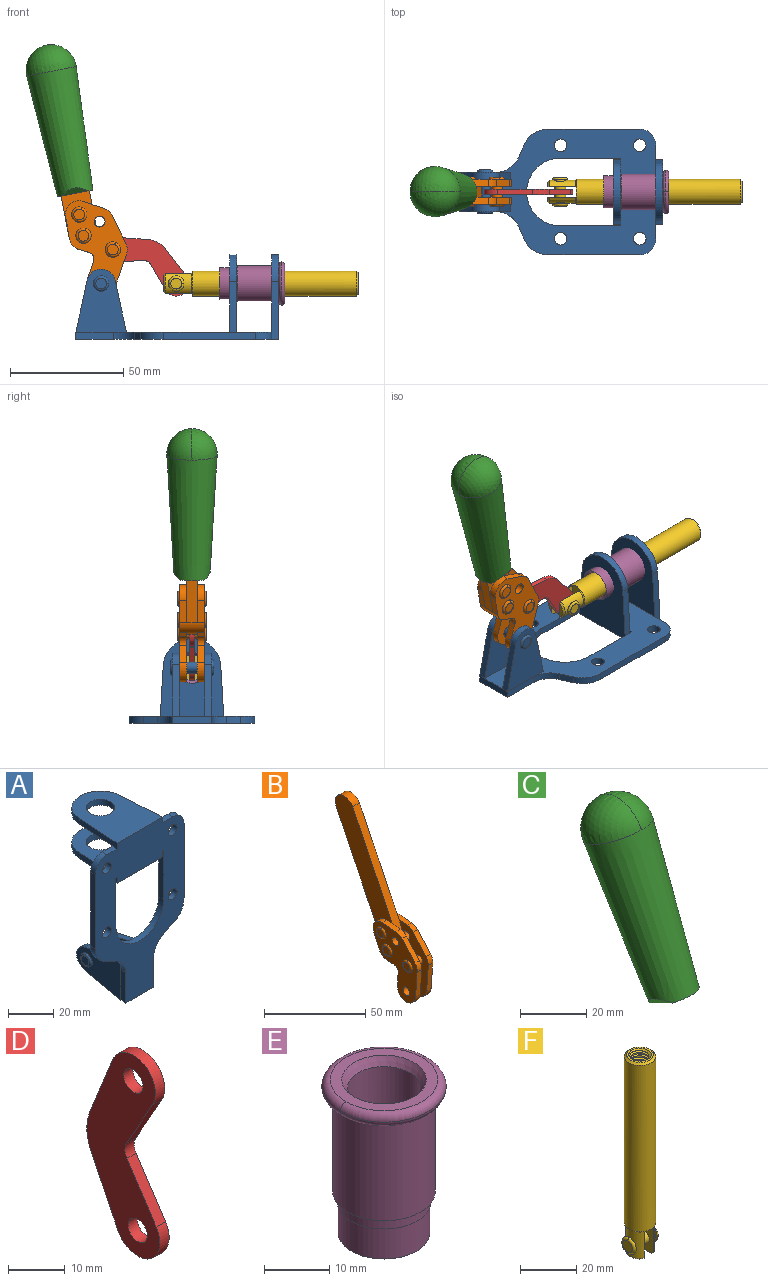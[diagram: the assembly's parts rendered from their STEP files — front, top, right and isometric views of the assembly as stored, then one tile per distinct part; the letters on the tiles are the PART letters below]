
ASSEMBLY  parts=6 mates=6
PART A: 55 faces, bbox 55.7x37.4x89.8 mm
  f0: torus R=2.41mm, axis (-1,0,0), area 15mm2, adj f11,f15,f25
  f1: torus R=2.41mm, axis (-1,0,0), area 15mm2, adj f10,f12,f22
  f2: cylinder r=2.78mm len=5.56mm, axis (0,-1,0), area 54.2mm2, adj f30,f54
  f3: cylinder r=14.99mm len=29.97mm, axis (0,-1,0), area 145.9mm2, adj f30,f49,f53,f54
  f4: cylinder r=2.78mm len=5.56mm, axis (0,-1,0), area 54.2mm2, adj f30,f54
  f5: cylinder r=2.78mm len=5.56mm, axis (0,-1,0), area 54.2mm2, adj f30,f54
  f6: cylinder r=2.78mm len=5.56mm, axis (0,-1,0), area 54.2mm2, adj f30,f54
  f7: cylinder r=6.35mm len=12.7mm, axis (0,0,1), area 123.6mm2, adj f27,f51
  f8: cylinder r=6.35mm len=12.7mm, axis (0,0,-1), area 124.7mm2, adj f21,f35
  f9: cylinder r=2.41mm len=11.18mm, axis (-1,0,0), area 169.4mm2, adj f16,f19
  f10: plane 4.83x4.83mm, normal (1,0,0), area 18.3mm2, adj f1,f12
  f11: plane 4.83x4.83mm, normal (-1,0,0), area 18.3mm2, adj f0,f15
  f12: torus R=2.41mm, axis (-1,0,0), area 15mm2, adj f1,f10,f22
  f13: cylinder r=6.35mm len=12.41mm, axis (1,0,0), area 53.4mm2, adj f18,f19,f22,f23
  f14: cylinder r=6.35mm len=12.41mm, axis (-1,0,0), area 53.4mm2, adj f16,f17,f24,f25
  f15: torus R=2.41mm, axis (-1,0,0), area 15mm2, adj f0,f11,f25
  f16: plane 27.86x22.35mm, normal (1,0,0), area 425.4mm2, adj f9,f14,f17,f24,f30
  f17: plane 22.86x4.97mm, normal (0,0.21,0.98), area 72.5mm2, adj f14,f16,f25,f30
  f18: plane 22.86x4.97mm, normal (0,0.21,0.98), area 72.5mm2, adj f13,f19,f22,f30
  f19: plane 27.86x22.35mm, normal (-1,0,0), area 425.4mm2, adj f9,f13,f18,f23,f30
  f20: cylinder r=12.7mm len=25.35mm, axis (0,0,-1), area 119.8mm2, adj f21,f34,f35,f36
  f21: plane 34.21x28.07mm, normal (0,0,-1), area 702.4mm2, adj f8,f20,f30,f34,f36
  f22: plane 27.96x22.45mm, normal (1,0,0), area 407.2mm2, adj f1,f12,f13,f18,f23,f30,f42,f43
  f23: plane 22.86x4.97mm, normal (0,0.21,-0.98), area 72.5mm2, adj f13,f19,f22,f44
  f24: plane 22.86x4.97mm, normal (0,0.21,-0.98), area 72.5mm2, adj f14,f16,f25,f44
  f25: plane 27.86x22.35mm, normal (-1,0,0), area 407.1mm2, adj f0,f14,f15,f17,f24,f30,f45,f46
  f26: plane 3.1x0.95mm, normal (0,0,-1), area 2.7mm2, adj f30,f49,f50,f54
  f27: plane 34.21x28.07mm, normal (0,0,1), area 702.4mm2, adj f7,f28,f30,f50,f52
  f28: cylinder r=12.7mm len=25.35mm, axis (0,0,1), area 118.8mm2, adj f27,f50,f51,f52
  f29: plane 3.1x0.95mm, normal (0,0,-1), area 2.7mm2, adj f30,f52,f53,f54
  f30: plane 86.54x55.63mm, normal (0,1,0), area 2362.9mm2, adj f2,f3,f4,f5,f6,f16,f17,f18
  f31: plane 40.56x3.1mm, normal (-1,0,0), area 125.7mm2, adj f30,f32,f48,f54
  f32: cylinder r=7.11mm len=7.11mm, axis (0,-1,0), area 34.6mm2, adj f30,f31,f33,f54
  f33: plane 6.67x3.1mm, normal (0,0,1), area 20.4mm2, adj f30,f32,f34,f54
  f34: plane 25.39x3.13mm, normal (-1,0.06,0), area 79.5mm2, adj f20,f21,f33,f35,f54
  f35: plane 37.31x28.45mm, normal (0,0,1), area 789.9mm2, adj f8,f20,f34,f36,f54
  f36: plane 25.39x3.13mm, normal (1,0.06,0), area 79.5mm2, adj f20,f21,f35,f37,f54
  f37: plane 6.67x3.1mm, normal (0,0,1), area 20.4mm2, adj f30,f36,f38,f54
  f38: cylinder r=7.11mm len=7.11mm, axis (0,-1,0), area 34.6mm2, adj f30,f37,f39,f54
  f39: plane 40.56x3.1mm, normal (1,0,0), area 125.7mm2, adj f30,f38,f40,f54
  f40: cylinder r=11.18mm len=10.16mm, axis (0,-1,0), area 39.5mm2, adj f30,f39,f41,f54
  f41: plane 6.09x3.1mm, normal (0.42,0,-0.91), area 20.8mm2, adj f30,f40,f42,f54
  f42: cylinder r=11.18mm len=9.41mm, axis (0,-1,0), area 37.2mm2, adj f22,f30,f41,f43,f54
  f43: plane 16.5x3.1mm, normal (1,0,0), area 51.1mm2, adj f22,f42,f44,f54
  f44: plane 17.37x3.1mm, normal (0,0,-1), area 53.8mm2, adj f23,f24,f30,f43,f45,f54
  f45: plane 16.5x3.1mm, normal (-1,0,0), area 51.1mm2, adj f25,f44,f46,f54
  f46: cylinder r=11.18mm len=9.41mm, axis (0,-1,0), area 37.2mm2, adj f25,f30,f45,f47,f54
  f47: plane 6.09x3.1mm, normal (-0.42,0,-0.91), area 20.8mm2, adj f30,f46,f48,f54
  f48: cylinder r=11.18mm len=10.16mm, axis (0,-1,0), area 39.5mm2, adj f30,f31,f47,f54
  f49: plane 26.54x3.1mm, normal (-1,0,0), area 82.3mm2, adj f3,f26,f30,f54
  f50: plane 25.39x3.1mm, normal (1,0.06,0), area 78.8mm2, adj f26,f27,f28,f51,f54
  f51: plane 37.31x28.45mm, normal (0,0,-1), area 789.9mm2, adj f7,f28,f50,f52,f54
  f52: plane 25.39x3.1mm, normal (-1,0.06,0), area 78.8mm2, adj f27,f28,f29,f51,f54
  f53: plane 26.54x3.1mm, normal (1,0,0), area 82.3mm2, adj f3,f29,f30,f54
  f54: plane 89.66x55.63mm, normal (0,-1,0), area 2678.5mm2, adj f2,f3,f4,f5,f6,f26,f29,f31
PART B: 59 faces, bbox 12.9x60.2x99.6 mm
  f0: torus R=2.39mm, axis (-1,0,0), area 14.9mm2, adj f20,f43,f51
  f1: torus R=2.39mm, axis (-1,0,0), area 14.9mm2, adj f19,f42,f51
  f2: torus R=2.39mm, axis (-1,0,0), area 14.9mm2, adj f18,f35,f51
  f3: torus R=2.39mm, axis (-1,0,0), area 14.9mm2, adj f14,f17,f23
  f4: torus R=2.39mm, axis (-1,0,0), area 14.9mm2, adj f13,f16,f23
  f5: torus R=2.39mm, axis (-1,0,0), area 14.9mm2, adj f12,f15,f23
  f6: cylinder r=2.39mm len=4.78mm, axis (1,0,0), area 46.5mm2, adj f48,f50,f51
  f7: cylinder r=2.39mm len=4.78mm, axis (1,0,0), area 46.5mm2, adj f50,f51
  f8: cylinder r=6.35mm len=12.68mm, axis (1,0,0), area 61.8mm2, adj f38,f39,f50,f51
  f9: cylinder r=2.39mm len=4.78mm, axis (-1,0,0), area 70.5mm2, adj f46,f50
  f10: cylinder r=2.39mm len=4.78mm, axis (-1,0,0), area 46.5mm2, adj f23,f45,f46
  f11: cylinder r=2.39mm len=4.78mm, axis (-1,0,0), area 46.5mm2, adj f23,f46
  f12: plane 4.78x4.78mm, normal (1,0,0), area 17.9mm2, adj f5,f15
  f13: plane 4.78x4.78mm, normal (1,0,0), area 17.9mm2, adj f4,f16
  f14: plane 4.78x4.78mm, normal (1,0,0), area 17.9mm2, adj f3,f17
  f15: torus R=2.39mm, axis (-1,0,0), area 14.9mm2, adj f5,f12,f23
  f16: torus R=2.39mm, axis (-1,0,0), area 14.9mm2, adj f4,f13,f23
  f17: torus R=2.39mm, axis (-1,0,0), area 14.9mm2, adj f3,f14,f23
  f18: plane 4.78x4.78mm, normal (-1,0,0), area 17.9mm2, adj f2,f35
  f19: plane 4.78x4.78mm, normal (-1,0,0), area 17.9mm2, adj f1,f42
  f20: plane 4.78x4.78mm, normal (-1,0,0), area 17.9mm2, adj f0,f43
  f21: plane 2.26x0.2mm, normal (1,0,0), area 0.2mm2, adj f31,f44
  f22: plane 2.26x0.2mm, normal (-1,0,0), area 0.2mm2, adj f41,f44
  f23: plane 39.37x30.77mm, normal (1,0,0), area 565.5mm2, adj f3,f4,f5,f10,f11,f15,f16,f17
  f24: cylinder r=6.1mm len=4.15mm, axis (-1,0,0), area 14.7mm2, adj f23,f25,f32,f46
  f25: plane 10.25x9.01mm, normal (0,-0.75,0.66), area 42.3mm2, adj f23,f24,f26,f46
  f26: cylinder r=6.35mm len=4.64mm, axis (-1,0,0), area 15.6mm2, adj f23,f25,f27,f46
  f27: plane 15.84x3.1mm, normal (0,-1,-0.07), area 49.2mm2, adj f23,f26,f28,f46
  f28: cylinder r=6.35mm len=12.68mm, axis (-1,0,0), area 61.8mm2, adj f23,f27,f29,f46
  f29: plane 8.11x3.1mm, normal (0,1,0.07), area 25.2mm2, adj f23,f28,f30,f46
  f30: cylinder r=3.05mm len=3.25mm, axis (-1,0,0), area 14.8mm2, adj f23,f29,f31,f46
  f31: plane 5.99x3.1mm, normal (0,0.07,-1), area 18.6mm2, adj f21,f23,f30,f44,f46
  f32: plane 9.5x3.1mm, normal (0,-0.07,1), area 29.5mm2, adj f23,f24,f33,f46,f47
  f33: cylinder r=6.1mm len=8.63mm, axis (-1,0,0), area 39.1mm2, adj f23,f32,f34,f47
  f34: plane 8.65x3.96mm, normal (0,0.91,-0.42), area 29.5mm2, adj f23,f33,f44,f47
  f35: torus R=2.39mm, axis (-1,0,0), area 14.9mm2, adj f2,f18,f51
  f36: plane 10.25x9.01mm, normal (0,-0.75,0.66), area 42.3mm2, adj f37,f49,f50,f51
  f37: cylinder r=6.35mm len=4.64mm, axis (1,0,0), area 15.6mm2, adj f36,f38,f50,f51
  f38: plane 15.84x3.1mm, normal (0,-1,-0.07), area 49.2mm2, adj f8,f37,f50,f51
  f39: plane 8.11x3.1mm, normal (0,1,0.07), area 25.2mm2, adj f8,f40,f50,f51
  f40: cylinder r=3.05mm len=3.25mm, axis (1,0,0), area 14.8mm2, adj f39,f41,f50,f51
  f41: plane 5.99x3.1mm, normal (0,0.07,-1), area 18.6mm2, adj f22,f40,f44,f50,f51
  f42: torus R=2.39mm, axis (-1,0,0), area 14.9mm2, adj f1,f19,f51
  f43: torus R=2.39mm, axis (-1,0,0), area 14.9mm2, adj f0,f20,f51
  f44: cylinder r=6.35mm len=12.12mm, axis (-1,0,0), area 128.9mm2, adj f21,f22,f23,f31,f34,f41,f46,f47
  f45: plane 2.65x1.35mm, normal (1,0,0), area 1mm2, adj f10,f55
  f46: plane 39.08x20.42mm, normal (-1,0,0), area 412.5mm2, adj f9,f10,f11,f24,f25,f26,f27,f28
  f47: plane 77.62x39.82mm, normal (1,0,0), area 850mm2, adj f32,f33,f34,f44,f53,f54,f55
  f48: plane 2.65x1.35mm, normal (-1,0,0), area 1mm2, adj f6,f55
  f49: cylinder r=6.1mm len=4.15mm, axis (1,0,0), area 14.7mm2, adj f36,f50,f51,f56
  f50: plane 39.08x20.42mm, normal (1,0,0), area 412.5mm2, adj f6,f7,f8,f9,f36,f37,f38,f39
  f51: plane 39.37x30.77mm, normal (-1,0,0), area 565.5mm2, adj f0,f1,f2,f6,f7,f8,f35,f36
  f52: plane 8.65x3.96mm, normal (0,0.91,-0.42), area 29.5mm2, adj f44,f51,f57,f58
  f53: plane 68.49x33.4mm, normal (0,0.9,-0.44), area 358.1mm2, adj f44,f47,f54,f58
  f54: cylinder r=6.35mm len=12.06mm, axis (1,0,0), area 93.7mm2, adj f47,f53,f55,f58
  f55: plane 68.49x33.4mm, normal (0,-0.9,0.44), area 358.1mm2, adj f44,f45,f46,f47,f48,f50,f54,f58
  f56: plane 9.5x3.1mm, normal (0,-0.07,1), area 29.5mm2, adj f49,f50,f51,f57,f58
  f57: cylinder r=6.1mm len=8.63mm, axis (1,0,0), area 39.1mm2, adj f51,f52,f56,f58
  f58: plane 77.62x39.82mm, normal (-1,0,0), area 850mm2, adj f44,f52,f53,f54,f55,f56,f57
PART C: 11 faces, bbox 22.3x42.6x64.5 mm
  f0: sphere r=11.13mm, area 411.4mm2, adj f1,f8
  f1: cone r=11.11mm half-angle=3.3deg, axis (0,0.44,0.9), area 3251.8mm2, adj f0,f7,f8,f9,f10
  f2: cylinder r=6.16mm len=11.7mm, axis (1,0,0), area 89.5mm2, adj f3,f4,f5,f6
  f3: plane 60.23x36.75mm, normal (-1,0,0), area 763.6mm2, adj f2,f4,f6,f10
  f4: plane 51.37x25.05mm, normal (0,0.9,-0.44), area 264.2mm2, adj f2,f3,f5,f10
  f5: plane 60.23x36.75mm, normal (1,0,0), area 763.6mm2, adj f2,f4,f6,f10
  f6: plane 51.37x25.05mm, normal (0,-0.9,0.44), area 264.2mm2, adj f2,f3,f5,f10
  f7: plane 9.95x5.95mm, normal (0.71,-0.31,-0.64), area 25.8mm2, adj f1,f10
  f8: sphere r=11.13mm, area 411.4mm2, adj f0,f1
  f9: plane 9.95x5.95mm, normal (-0.71,-0.31,-0.64), area 25.8mm2, adj f1,f10
  f10: plane 14.27x11.38mm, normal (0,-0.44,-0.9), area 106.7mm2, adj f1,f3,f4,f5,f6,f7,f9
PART D: 12 faces, bbox 2.3x18.2x42.8 mm
  f0: cylinder r=2.4mm len=4.8mm, axis (1,0,0), area 34.9mm2, adj f4,f11
  f1: cylinder r=10.41mm len=8.47mm, axis (1,0,0), area 20.2mm2, adj f4,f9,f10,f11
  f2: cylinder r=3.05mm len=3.16mm, axis (1,0,0), area 7.7mm2, adj f4,f6,f7,f11
  f3: cylinder r=2.4mm len=4.8mm, axis (1,0,0), area 34.9mm2, adj f4,f11
  f4: plane 42.81x18.23mm, normal (-1,0,0), area 414.1mm2, adj f0,f1,f2,f3,f5,f6,f7,f8
  f5: cylinder r=5.54mm len=10.67mm, axis (1,0,0), area 41.8mm2, adj f4,f6,f10,f11
  f6: plane 11.66x6.53mm, normal (0,-0.87,-0.49), area 30.9mm2, adj f2,f4,f5,f11
  f7: plane 11.17x7.33mm, normal (0,-0.84,0.55), area 30.9mm2, adj f2,f4,f8,f11
  f8: cylinder r=5.54mm len=10.51mm, axis (1,0,0), area 41.8mm2, adj f4,f7,f9,f11
  f9: plane 13.67x6.67mm, normal (0,0.9,-0.44), area 35.1mm2, adj f1,f4,f8,f11
  f10: plane 14.1x5.7mm, normal (0,0.93,0.37), area 35.1mm2, adj f1,f4,f5,f11
  f11: plane 42.81x18.23mm, normal (1,0,0), area 414.1mm2, adj f0,f1,f2,f3,f5,f6,f7,f8
PART E: 15 faces, bbox 20.6x20.6x28.7 mm
  f0: torus R=8.26mm, axis (0,0,1), area 56.8mm2, adj f1,f10,f12
  f1: torus R=8.26mm, axis (0,0,1), area 56.8mm2, adj f0,f6,f13
  f2: cylinder r=5.59mm len=25.91mm, axis (0,0,1), area 909.6mm2, adj f3,f4
  f3: cone r=6.86mm half-angle=45deg, axis (0,0,-1), area 70.2mm2, adj f2,f14
  f4: cone r=6.47mm half-angle=30deg, axis (0,0,1), area 66.7mm2, adj f2,f13
  f5: cylinder r=7.04mm len=14.07mm, axis (0,0,1), area 252.6mm2, adj f11,f14
  f6: torus R=8.26mm, axis (0,0,1), area 56.8mm2, adj f1,f12,f13
  f7: cylinder r=7.16mm len=14.33mm, axis (0,0,1), area 91.5mm2, adj f9,f11
  f8: cylinder r=7.86mm len=18.42mm, axis (0,0,1), area 909.6mm2, adj f9,f10
  f9: plane 15.72x15.72mm, normal (0,0,-1), area 33mm2, adj f7,f8
  f10: plane 16.51x16.51mm, normal (0,0,-1), area 19.9mm2, adj f0,f8,f12
  f11: plane 14.33x14.33mm, normal (0,0,-1), area 5.7mm2, adj f5,f7
  f12: torus R=8.26mm, axis (0,0,1), area 56.8mm2, adj f0,f6,f10
  f13: plane 16.51x16.51mm, normal (0,0,1), area 82.7mm2, adj f1,f4,f6
  f14: plane 14.07x14.07mm, normal (0,0,-1), area 7.8mm2, adj f3,f5
PART F: 48 faces, bbox 12.6x11.1x86.1 mm
  f0: torus R=2.41mm, axis (-1,0,0), area 15mm2, adj f30,f32,f34
  f1: torus R=2.41mm, axis (-1,0,0), area 15mm2, adj f29,f31,f33
  f2: cylinder r=5.54mm len=72.39mm, axis (0,0,1), area 2518.5mm2, adj f3,f4,f42,f43
  f3: cone r=5.54mm half-angle=45deg, axis (0,0,1), area 7.6mm2, adj f2,f5,f41
  f4: cone r=5.54mm half-angle=45deg, axis (0,0,-1), area 34.9mm2, adj f2,f39
  f5: cylinder r=5.08mm len=11.48mm, axis (0,0,1), area 108.3mm2, adj f3,f7,f8,f41
  f6: cylinder r=2.41mm len=4.83mm, axis (-1,0,0), area 71.2mm2, adj f40,f41
  f7: cylinder r=2.41mm len=4.83mm, axis (-1,0,0), area 7.6mm2, adj f5,f34
  f8: cone r=5.08mm half-angle=45deg, axis (0,0,1), area 10.6mm2, adj f5,f37,f41
  f9: cone r=3.98mm half-angle=45deg, axis (0,0,1), area 17.6mm2, adj f27,f39,f45,f46,f47
  f10: cylinder r=2.41mm len=4.83mm, axis (-1,0,0), area 7.6mm2, adj f33,f38
  f11: cylinder r=3.2mm len=6.4mm, axis (0,0,1), area 78.4mm2, adj f12,f28,f44,f45,f47
  f12: cylinder r=3.2mm len=6.4mm, axis (0,0,1), area 10.5mm2, adj f11,f13,f45,f47
  f13: cylinder r=3.2mm len=6.4mm, axis (0,0,1), area 10.5mm2, adj f12,f14,f45,f47
  f14: cylinder r=3.2mm len=6.4mm, axis (0,0,1), area 10.5mm2, adj f13,f15,f45,f47
  f15: cylinder r=3.2mm len=6.4mm, axis (0,0,1), area 10.5mm2, adj f14,f16,f45,f47
  f16: cylinder r=3.2mm len=6.4mm, axis (0,0,1), area 10.5mm2, adj f15,f17,f45,f47
  f17: cylinder r=3.2mm len=6.4mm, axis (0,0,1), area 10.5mm2, adj f16,f18,f45,f47
  f18: cylinder r=3.2mm len=6.4mm, axis (0,0,1), area 10.5mm2, adj f17,f19,f45,f47
  f19: cylinder r=3.2mm len=6.4mm, axis (0,0,1), area 10.5mm2, adj f18,f20,f45,f47
  f20: cylinder r=3.2mm len=6.4mm, axis (0,0,1), area 10.5mm2, adj f19,f21,f45,f47
  f21: cylinder r=3.2mm len=6.4mm, axis (0,0,1), area 10.5mm2, adj f20,f22,f45,f47
  f22: cylinder r=3.2mm len=6.4mm, axis (0,0,1), area 10.5mm2, adj f21,f23,f45,f47
  f23: cylinder r=3.2mm len=6.4mm, axis (0,0,1), area 10.5mm2, adj f22,f24,f45,f47
  f24: cylinder r=3.2mm len=6.4mm, axis (0,0,1), area 10.5mm2, adj f23,f25,f45,f47
  f25: cylinder r=3.2mm len=6.4mm, axis (0,0,1), area 10.5mm2, adj f24,f26,f45,f47
  f26: cylinder r=3.2mm len=6.4mm, axis (0,0,1), area 10.5mm2, adj f25,f27,f45,f47
  f27: cylinder r=3.2mm len=6.4mm, axis (0,0,1), area 7.4mm2, adj f9,f26,f45,f47
  f28: cone r=3.2mm half-angle=60deg, axis (0,0,1), area 37.2mm2, adj f11
  f29: plane 4.83x4.83mm, normal (-1,0,0), area 18.3mm2, adj f1,f31
  f30: plane 4.83x4.83mm, normal (1,0,0), area 18.3mm2, adj f0,f32
  f31: torus R=2.41mm, axis (-1,0,0), area 15mm2, adj f1,f29,f33
  f32: torus R=2.41mm, axis (-1,0,0), area 15mm2, adj f0,f30,f34
  f33: plane 6.83x6.83mm, normal (1,0,0), area 18.3mm2, adj f1,f10,f31
  f34: plane 6.83x6.83mm, normal (-1,0,0), area 18.3mm2, adj f0,f7,f32
  f35: cone r=5.08mm half-angle=45deg, axis (0,0,1), area 10.6mm2, adj f36,f38,f40
  f36: plane 7.25x1.97mm, normal (0,0,-1), area 10mm2, adj f35,f40
  f37: plane 7.25x1.97mm, normal (0,0,-1), area 10mm2, adj f8,f41
  f38: cylinder r=5.08mm len=11.48mm, axis (0,0,1), area 108.3mm2, adj f10,f35,f40,f42
  f39: plane 9.55x9.55mm, normal (0,0,1), area 22mm2, adj f4,f9
  f40: plane 12.76x10.09mm, normal (1,0,0), area 95.7mm2, adj f6,f35,f36,f38,f42,f43
  f41: plane 12.76x10.09mm, normal (-1,0,0), area 95.7mm2, adj f3,f5,f6,f8,f37,f43
  f42: cone r=5.54mm half-angle=45deg, axis (0,0,1), area 7.6mm2, adj f2,f38,f40
  f43: plane 11.07x4.7mm, normal (0,0,-1), area 50.4mm2, adj f2,f40,f41
  f44: plane 0.89x0.62mm, normal (-1,0,0), area 0.3mm2, adj f11,f45,f46,f47
  f45: bspline ~24.8x7.63mm, area 266.6mm2, adj f9,f11,f12,f13,f14,f15,f16,f17
  f46: bspline ~24.87x7.63mm, area 73.6mm2, adj f9,f44,f45,f47
  f47: bspline ~24.98x7.63mm, area 272.5mm2, adj f9,f11,f12,f13,f14,f15,f16,f17
PLACE A rot(axis=(0.58,0.58,0.58),120deg) t=(0,0,0)mm fixed
PLACE B rot(axis=(0.13,0.13,0.98),91deg) t=(-0.01,0,49.24)mm
PLACE C rot(axis=(0.13,0.13,0.98),91deg) t=(-0.01,0,49.24)mm
PLACE D rot(axis=(0.47,-0.47,-0.75),106.2deg) t=(-23.91,0,10.71)mm
PLACE E rot(axis=(0.71,0,0.71),180deg) t=(0,24.61,24.61)mm
PLACE F rot(axis=(0.58,0.58,0.58),120deg) t=(-14.42,0,0)mm
MATE fastened E.f0 <-> A.f7  axis (-1,0,0) through (46.39,0,24.61)mm
MATE revolute F.f6 <-> D.f3  axis (0,-1,0) through (1.05,0,24.61)mm
MATE revolute B.f7 <-> A.f0  axis (0,-1,0) through (-32.09,0,24.61)mm
MATE slider F.f2 <-> E.f2  axis (1,0,0) through (44.36,0,24.61)mm
MATE fastened C.f2 <-> B.f54  axis (0,1,0) through (-54.46,0,120.54)mm
MATE revolute D.f5 <-> B.f4  axis (0,-1,0) through (-26.92,0,39.62)mm
